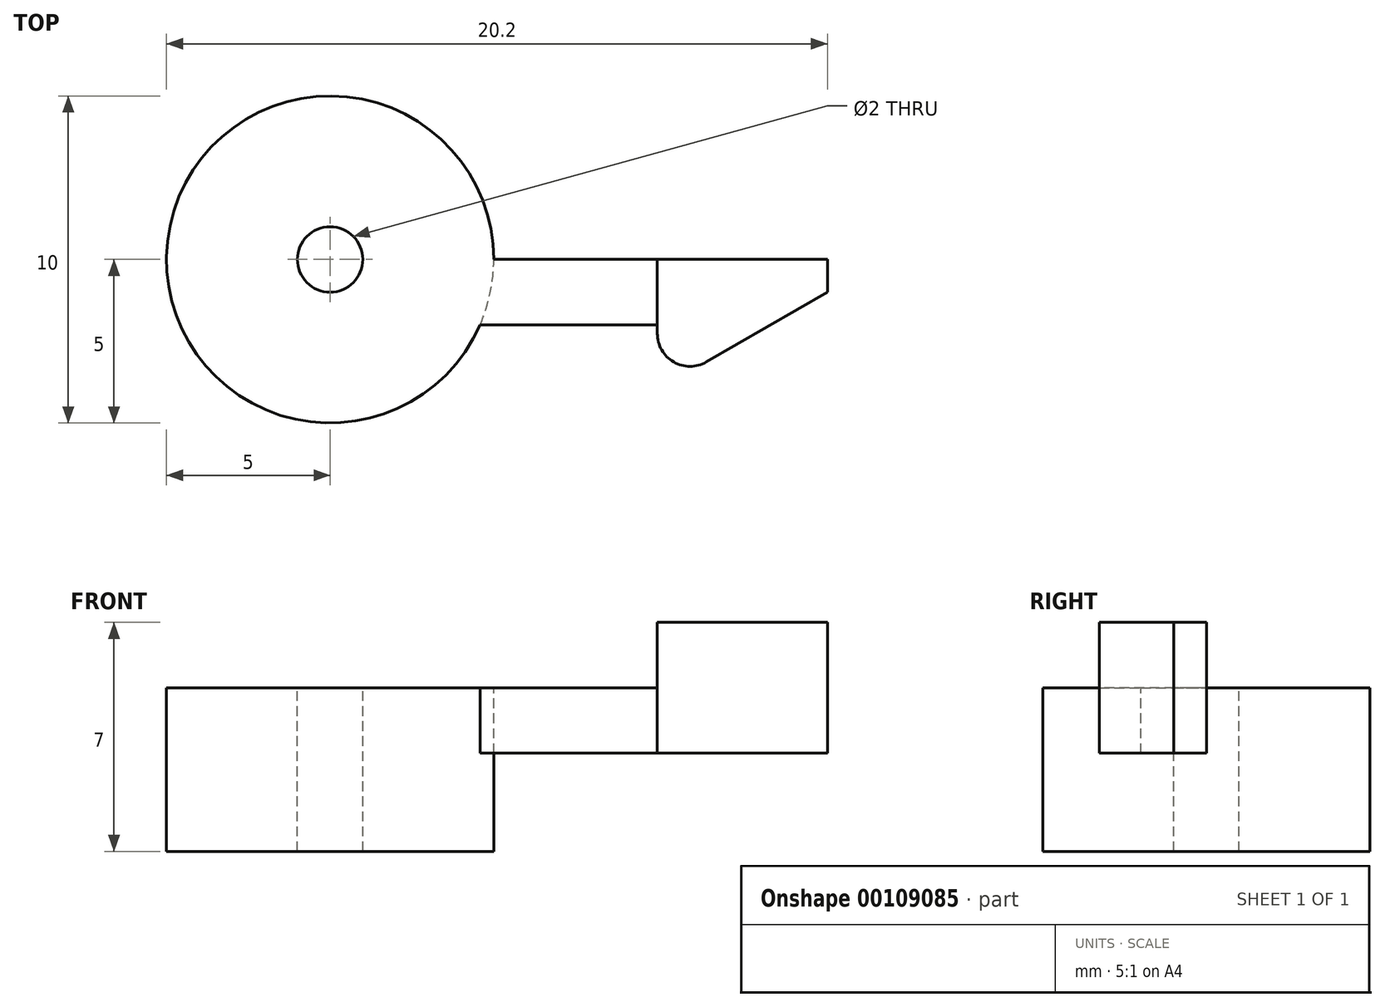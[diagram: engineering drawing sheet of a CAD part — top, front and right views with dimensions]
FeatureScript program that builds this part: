
annotation { "Feature Type Name" : "Feature", "Feature Type Description" : "" }
export const myFeature = defineFeature(function(context is Context, id is Id, definition is map)
    precondition{}
    {
        {
            var Q0;
            Q0=qCreatedBy(makeId("Top.planeOp"),FACE);
            var sketch = newSketch(context, id + "F0", { "sketchPlane" : qUnion([Q0])});
            skCircle(sketch, "E0", {"center": v(0, 0) * mm, "radius": 5 * mm});
            skLineSegment(sketch, "E1", {"start": v(10, 0) * mm, "end": v(5, 0) * mm});
            skLineSegment(sketch, "E2", {"start": v(15.2, 0) * mm, "end": v(10, 0) * mm});
            skLineSegment(sketch, "E3.MirrorCS", {"start": v(10, -2) * mm, "end": v(4.58, -2) * mm});
            skLineSegment(sketch, "E4.MirrorCS", {"start": v(10, -2) * mm, "end": v(10, -4) * mm});
            skLineSegment(sketch, "E5.MirrorCS", {"start": v(10, -4) * mm, "end": v(15.2, -1) * mm});
            skLineSegment(sketch, "E6.MirrorCS", {"start": v(15.2, -1) * mm, "end": v(15.2, 0) * mm});
            skLineSegment(sketch, "E7", {"start": v(10, -2) * mm, "end": v(10, 0) * mm});
            skSolve(sketch);
        }
        {
            var Q0;
            {var subQ0=sQuery(id+"F0.wireOp",EDGE,"E0");var subQ1=makeQuery(id+"F0.imprint","INTERSECT",VERTEX,{"derivedFrom":[subQ0,sQuery(id+"F0.wireOp",EDGE,"E1")]});Q0=makeQuery(id+"F0.imprint","IMPRINT",FACE,{"disambiguationData":[TD([[makeQuery(id+"F0.imprint","IMPRINT",EDGE,{"disambiguationData":[TD([[subQ1,-1.0]])],"derivedFrom":subQ0}),1.0]])]});}
            extrude(context, id + "F1", {"entities" : qUnion([Q0]), "oppositeDirection" : true, "depth" : 5 * mm});
        }
        {
            var Q0;
            {var subQ0=sQuery(id+"F0.wireOp",EDGE,"E1");Q0=makeQuery(id+"F0.imprint","IMPRINT",FACE,{"disambiguationData":[TD([[makeQuery(id+"F0.imprint","IMPRINT",EDGE,{"derivedFrom":subQ0}),1.0]])]});}
            extrude(context, id + "F2", {"entities" : qUnion([Q0]), "operationType" : NewBodyOperationType.ADD, "oppositeDirection" : true, "depth" : 2 * mm});
        }
        {
            var Q0;
            Q0=makeQuery(id+"F0.imprint","IMPRINT",FACE,{"disambiguationData":[TD([[makeQuery(id+"F0.imprint","IMPRINT",EDGE,{"derivedFrom":sQuery(id+"F0.wireOp",EDGE,"E2")}),1.0]])]});
            extrude(context, id + "F3", {"entities" : qUnion([Q0]), "operationType" : NewBodyOperationType.ADD, "endBound" : BoundingType.SYMMETRIC, "depth" : 4 * mm});
        }
        {
            var Q0;
            Q0=makeQuery(id+"F3.opExtrude","SWEPT_EDGE",EDGE,{"disambiguationData":[OSD([sQuery(id+"F0.wireOp",EDGE,"E4.MirrorCS"),sQuery(id+"F0.wireOp",EDGE,"E5.MirrorCS")])]});
            fillet(context, id + "F4", {"entities" : qUnion([Q0]), "radius" : 1 * mm, "tangentPropagation" : true, "allowEdgeOverflow" : false});
        }
        {
            var Q0;
            Q0=sQuery(id+"F0.wireOp",VERTEX,"E0.center");
            var Q1;
            Q1=makeQuery(id+"F1.opExtrude","SWEPT_BODY",BODY,{"disambiguationData":[OSD([sQuery(id+"F0.wireOp",EDGE,"E0")])]});
            hole(context, id + "F5", {"style" : HoleStyle.SIMPLE, "endStyle" : HoleEndStyle.THROUGH, "holeDiameter" : 2 * mm, "locations" : qUnion([Q0]), "scope" : qUnion([Q1]), "isTappedThrough" : true});
        }
    });
